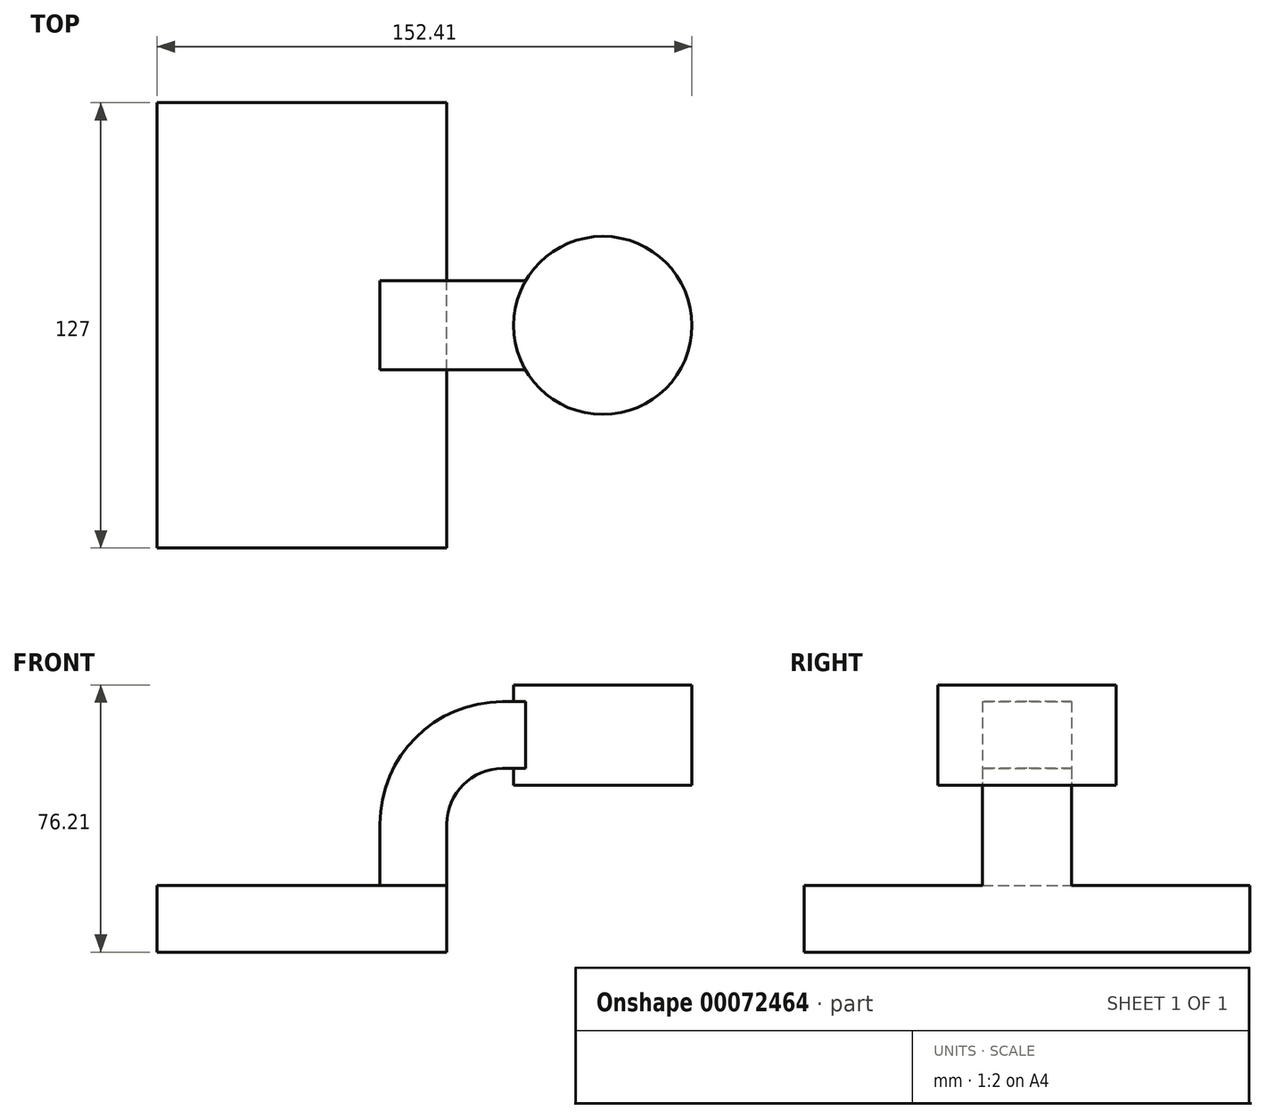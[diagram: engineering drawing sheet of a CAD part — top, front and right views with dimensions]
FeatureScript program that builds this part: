
annotation { "Feature Type Name" : "Feature", "Feature Type Description" : "" }
export const myFeature = defineFeature(function(context is Context, id is Id, definition is map)
    precondition{}
    {
        {
            var Q0;
            Q0=qCreatedBy(makeId("Front.planeOp"),FACE);
            var sketch = newSketch(context, id + "F0", { "sketchPlane" : qUnion([Q0])});
            skLineSegment(sketch, "E0.rect.bottom", {"start": v(41.28, -9.52) * mm, "end": v(-41.28, -9.53) * mm});
            skLineSegment(sketch, "E0.rect.top", {"start": v(41.28, 9.53) * mm, "end": v(-41.28, 9.53) * mm});
            skLineSegment(sketch, "E0.rect.left", {"start": v(41.28, -9.52) * mm, "end": v(41.28, 9.53) * mm});
            skLineSegment(sketch, "E0.rect.right", {"start": v(-41.28, -9.53) * mm, "end": v(-41.28, 9.53) * mm});
            skPoint(sketch, "E0.rect.middle", {"position": v(0, 0) * mm});
            skLineSegment(sketch, "E1.rect.bottom", {"start": v(111.12, 38.1) * mm, "end": v(60.33, 38.1) * mm});
            skLineSegment(sketch, "E1.rect.top", {"start": v(111.13, 66.68) * mm, "end": v(60.33, 66.68) * mm});
            skLineSegment(sketch, "E1.rect.left", {"start": v(111.13, 38.1) * mm, "end": v(111.13, 66.68) * mm});
            skLineSegment(sketch, "E1.rect.right", {"start": v(60.33, 38.1) * mm, "end": v(60.33, 66.68) * mm});
            skPoint(sketch, "E1.rect.middle", {"position": v(85.72, 52.39) * mm});
            skLineSegment(sketch, "E2", {"start": v(41.28, 9.53) * mm, "end": v(41.28, 26.97) * mm});
            skArc(sketch, "E3", {"start": v(41.27, 26.97) * mm, "mid": v(45.92, 38.2) * mm, "end": v(57.15, 42.85) * mm});
            skLineSegment(sketch, "E4", {"start": v(57.15, 42.85) * mm, "end": v(85.72, 42.85) * mm});
            skPoint(sketch, "E4.endSnap0", {"position": v(85.72, 38.1) * mm});
            skLineSegment(sketch, "E5.0", {"start": v(57.15, 61.9) * mm, "end": v(85.72, 61.9) * mm});
            skArc(sketch, "E5.1", {"start": v(22.22, 26.97) * mm, "mid": v(32.45, 51.67) * mm, "end": v(57.15, 61.9) * mm});
            skLineSegment(sketch, "E5.2", {"start": v(22.22, 9.53) * mm, "end": v(22.22, 26.97) * mm});
            skLineSegment(sketch, "E6", {"start": v(85.72, 38.1) * mm, "end": v(85.72, 66.68) * mm});
            skFitSpline(sketch, "E7", {"points": [v(-41.28, 9.53) * mm, v(57.15, 61.9) * mm], "startDerivative": vector(10.86, 103.94) * mm, "endDerivative": vector(128.2, -0.86) * mm});
            skSolve(sketch);
        }
        {
            var Q0;
            Q0=makeQuery(id+"F0.imprint","IMPRINT",FACE,{"disambiguationData":[TD([[makeQuery(id+"F0.imprint","IMPRINT",EDGE,{"derivedFrom":sQuery(id+"F0.wireOp",EDGE,"E0.rect.bottom")}),-1.0]])]});
            extrude(context, id + "F1", {"entities" : qUnion([Q0]), "endBound" : BoundingType.SYMMETRIC, "depth" : 127 * mm});
        }
        {
            var Q0;
            {var subQ1=sQuery(id+"F0.wireOp",EDGE,"E2");Q0=makeQuery(id+"F0.imprint","IMPRINT",FACE,{"disambiguationData":[TD([[makeQuery(id+"F0.imprint","IMPRINT",EDGE,{"derivedFrom":subQ1}),1.0]])]});}
            var Q1;
            {var subQ0=sQuery(id+"F0.wireOp",EDGE,"E4");var subQ1=sQuery(id+"F0.wireOp",EDGE,"E1.rect.right");var subQ2=makeQuery(id+"F0.imprint","INTERSECT",VERTEX,{"derivedFrom":[subQ1,subQ0]});Q1=makeQuery(id+"F0.imprint","IMPRINT",FACE,{"disambiguationData":[TD([[makeQuery(id+"F0.imprint","IMPRINT",EDGE,{"disambiguationData":[TD([[subQ2,-1.0]])],"derivedFrom":subQ1}),-1.0]])]});}
            extrude(context, id + "F2", {"entities" : qUnion([Q0, Q1]), "operationType" : NewBodyOperationType.ADD, "endBound" : BoundingType.SYMMETRIC, "depth" : 25.4 * mm});
        }
        {
            var Q0;
            Q0=makeQuery(id+"F0.imprint","IMPRINT",FACE,{"disambiguationData":[TD([[makeQuery(id+"F0.imprint","IMPRINT",EDGE,{"derivedFrom":sQuery(id+"F0.wireOp",EDGE,"E5.1")}),1.0]])]});
            extrude(context, id + "F3", {"entities" : qUnion([Q0]), "operationType" : NewBodyOperationType.ADD, "endBound" : BoundingType.SYMMETRIC, "depth" : 12.7 * mm});
        }
        {
            var Q0;
            {var subQ0=sQuery(id+"F0.wireOp",EDGE,"E1.rect.left");Q0=makeQuery(id+"F0.imprint","IMPRINT",FACE,{"disambiguationData":[TD([[makeQuery(id+"F0.imprint","IMPRINT",EDGE,{"derivedFrom":subQ0}),1.0]])]});}
            var Q1;
            Q1=sQuery(id+"F0.wireOp",EDGE,"E6");
            revolve(context, id + "F4", {"operationType" : NewBodyOperationType.ADD, "entities" : qUnion([Q0]), "axis" : qUnion([Q1]), "revolveType" : RevolveType.FULL});
        }
    });
